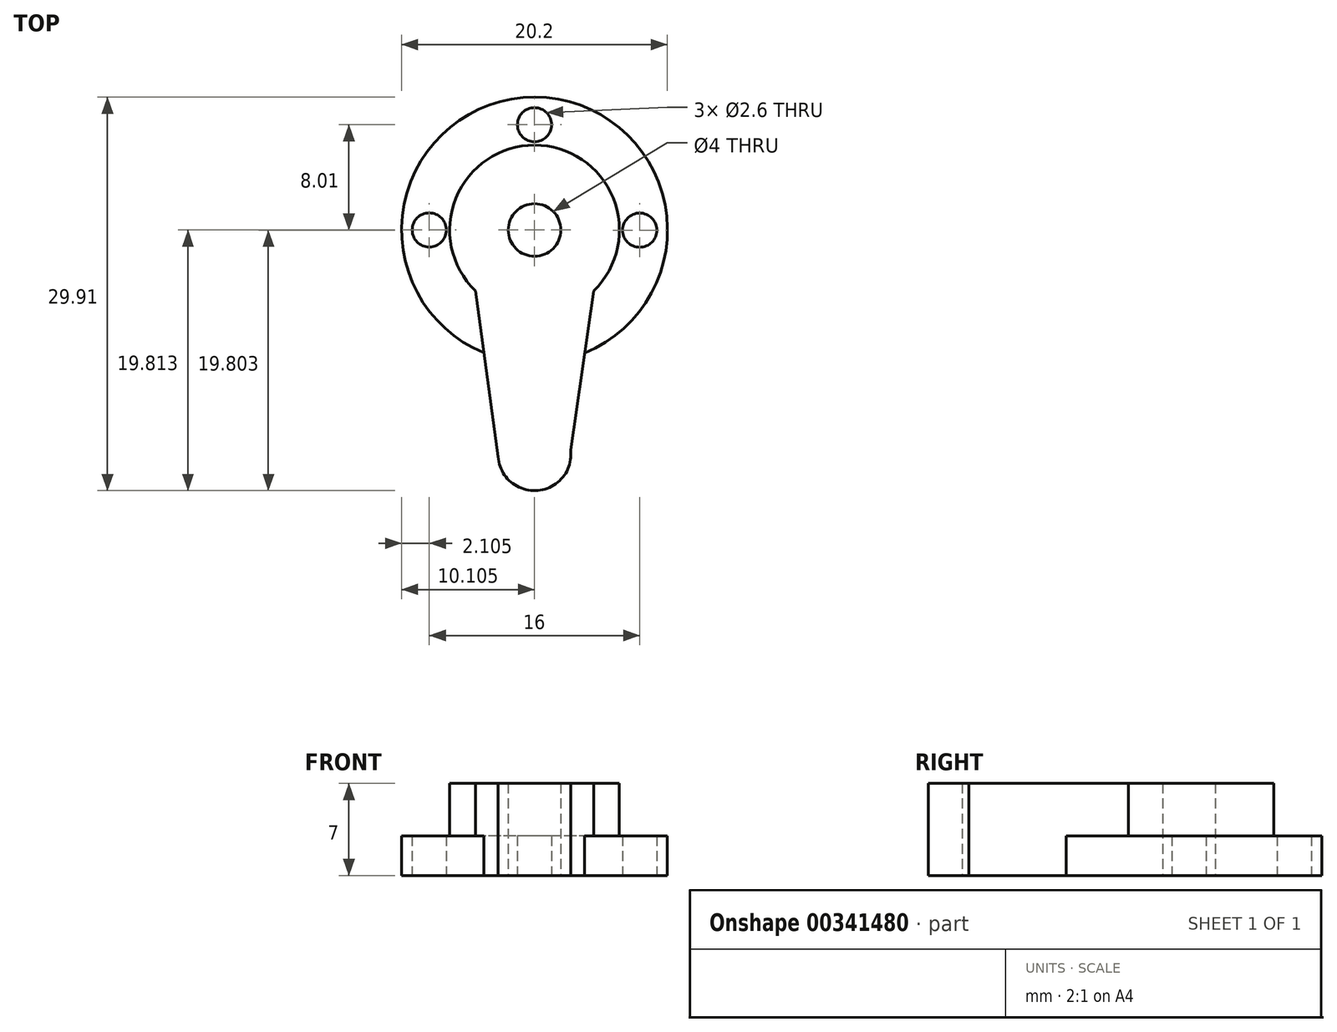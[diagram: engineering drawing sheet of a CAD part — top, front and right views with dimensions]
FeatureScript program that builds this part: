
annotation { "Feature Type Name" : "Feature", "Feature Type Description" : "" }
export const myFeature = defineFeature(function(context is Context, id is Id, definition is map)
    precondition{}
    {
        {
            var Q0;
            Q0=qCreatedBy(makeId("Top.planeOp"),FACE);
            var sketch = newSketch(context, id + "F0", { "sketchPlane" : qUnion([Q0])});
            skCircle(sketch, "E0", {"center": v(-1.19, 10.76) * mm, "radius": 2.77 * mm});
            skPoint(sketch, "E0.first.point", {"position": v(0, 13.26) * mm});
            skPoint(sketch, "E0.second.point", {"position": v(0, 8.26) * mm});
            skPoint(sketch, "E0.third.point", {"position": v(0.69, 8.72) * mm});
            skCircle(sketch, "E1", {"center": v(-1.19, 27.81) * mm, "radius": 6.45 * mm});
            skPoint(sketch, "E1.first.point", {"position": v(-1.19, 34.26) * mm});
            skPoint(sketch, "E1.second.point", {"position": v(-1.19, 21.36) * mm});
            skPoint(sketch, "E1.third.point", {"position": v(4.49, 24.74) * mm});
            skLineSegment(sketch, "E2", {"start": v(-5.69, 23.2) * mm, "end": v(3.31, 23.2) * mm});
            skLineSegment(sketch, "E3", {"start": v(-3.95, 10.57) * mm, "end": v(-5.69, 23.2) * mm});
            skLineSegment(sketch, "E4", {"start": v(1.56, 11.08) * mm, "end": v(3.31, 23.2) * mm});
            skCircle(sketch, "E5", {"center": v(-1.19, 27.81) * mm, "radius": 2 * mm});
            skCircle(sketch, "E6", {"center": v(-1.19, 27.81) * mm, "radius": 10.1 * mm});
            skCircle(sketch, "E7", {"center": v(-1.19, 27.81) * mm, "radius": 8 * mm});
            skCircle(sketch, "E8", {"center": v(-1.19, 35.81) * mm, "radius": 1.3 * mm});
            skLineSegment(sketch, "E9", {"start": v(-1.31, 27.81) * mm, "end": v(5.26, 27.81) * mm});
            skLineSegment(sketch, "E10", {"start": v(5.26, 27.81) * mm, "end": v(6.81, 27.8) * mm});
            skLineSegment(sketch, "E11", {"start": v(-1.19, 27.81) * mm, "end": v(-9.19, 27.81) * mm});
            skCircle(sketch, "E12", {"center": v(6.81, 27.8) * mm, "radius": 1.3 * mm});
            skCircle(sketch, "E13", {"center": v(-9.19, 27.81) * mm, "radius": 1.3 * mm});
            skLineSegment(sketch, "E14", {"start": v(-1.19, 27.81) * mm, "end": v(-1.19, 10.76) * mm});
            skSolve(sketch);
        }
        {
            var Q0;
            {var subQ0=sQuery(id+"F0.wireOp",EDGE,"E2");Q0=makeQuery(id+"F0.imprint","IMPRINT",FACE,{"disambiguationData":[TD([[makeQuery(id+"F0.imprint","IMPRINT",EDGE,{"derivedFrom":subQ0}),-1.0]])]});}
            var Q1;
            {var subQ0=sQuery(id+"F0.wireOp",EDGE,"E2");Q1=makeQuery(id+"F0.imprint","IMPRINT",FACE,{"disambiguationData":[TD([[makeQuery(id+"F0.imprint","IMPRINT",EDGE,{"derivedFrom":subQ0}),1.0]])]});}
            var Q2;
            {var subQ0=sQuery(id+"F0.wireOp",EDGE,"E3");var subQ1=sQuery(id+"F0.wireOp",EDGE,"E0");var subQ2=makeQuery(id+"F0.imprint","INTERSECT",VERTEX,{"derivedFrom":[subQ1,subQ0]});Q2=makeQuery(id+"F0.imprint","IMPRINT",FACE,{"disambiguationData":[TD([[makeQuery(id+"F0.imprint","IMPRINT",EDGE,{"disambiguationData":[TD([[subQ2,1.0]])],"derivedFrom":subQ1}),-1.0]])]});}
            var Q3;
            {var subQ0=sQuery(id+"F0.wireOp",EDGE,"E0");var subQ1=makeQuery(id+"F0.imprint","INTERSECT",VERTEX,{"derivedFrom":[subQ0,sQuery(id+"F0.wireOp",EDGE,"E3")]});Q3=makeQuery(id+"F0.imprint","IMPRINT",FACE,{"disambiguationData":[TD([[makeQuery(id+"F0.imprint","IMPRINT",EDGE,{"disambiguationData":[TD([[subQ1,1.0]])],"derivedFrom":subQ0}),1.0]])]});}
            var Q4;
            {var subQ0=sQuery(id+"F0.wireOp",EDGE,"E6");var subQ1=sQuery(id+"F0.wireOp",EDGE,"E3");var subQ2=makeQuery(id+"F0.imprint","INTERSECT",VERTEX,{"derivedFrom":[subQ1,subQ0]});Q4=makeQuery(id+"F0.imprint","IMPRINT",FACE,{"disambiguationData":[TD([[makeQuery(id+"F0.imprint","IMPRINT",EDGE,{"disambiguationData":[TD([[subQ2,-1.0]])],"derivedFrom":subQ1}),-1.0]])]});}
            var Q5;
            {var subQ0=sQuery(id+"F0.wireOp",EDGE,"E3");var subQ6=sQuery(id+"F0.wireOp",EDGE,"E7");var subQ7=makeQuery(id+"F0.imprint","INTERSECT",VERTEX,{"derivedFrom":[subQ0,subQ6]});Q5=makeQuery(id+"F0.imprint","IMPRINT",FACE,{"disambiguationData":[TD([[makeQuery(id+"F0.imprint","IMPRINT",EDGE,{"disambiguationData":[TD([[subQ7,-1.0]])],"derivedFrom":subQ6}),1.0]])]});}
            var Q6;
            {var subQ5=sQuery(id+"F0.wireOp",EDGE,"E1");var subQ8=sQuery(id+"F0.wireOp",EDGE,"E12");var subQ10=makeQuery(id+"F0.imprint","INTERSECT",VERTEX,{"disambiguationData":[OD(0.0)],"derivedFrom":[subQ5,subQ8]});Q6=makeQuery(id+"F0.imprint","IMPRINT",FACE,{"disambiguationData":[TD([[makeQuery(id+"F0.imprint","IMPRINT",EDGE,{"disambiguationData":[TD([[subQ10,-1.0]])],"derivedFrom":subQ5}),1.0]])]});}
            var Q7;
            {var subQ0=sQuery(id+"F0.wireOp",EDGE,"E9");var subQ1=sQuery(id+"F0.wireOp",EDGE,"E5");var subQ2=makeQuery(id+"F0.imprint","INTERSECT",VERTEX,{"derivedFrom":[subQ1,subQ0]});Q7=makeQuery(id+"F0.imprint","IMPRINT",FACE,{"disambiguationData":[TD([[makeQuery(id+"F0.imprint","IMPRINT",EDGE,{"disambiguationData":[TD([[subQ2,1.0]])],"derivedFrom":subQ1}),-1.0]])]});}
            var Q8;
            {var subQ0=sQuery(id+"F0.wireOp",EDGE,"E4");var subQ1=sQuery(id+"F0.wireOp",EDGE,"E0");var subQ2=makeQuery(id+"F0.imprint","INTERSECT",VERTEX,{"derivedFrom":[subQ1,subQ0]});Q8=makeQuery(id+"F0.imprint","IMPRINT",FACE,{"disambiguationData":[TD([[makeQuery(id+"F0.imprint","IMPRINT",EDGE,{"disambiguationData":[TD([[subQ2,-1.0]])],"derivedFrom":subQ1}),-1.0]])]});}
            var Q9;
            {var subQ0=sQuery(id+"F0.wireOp",EDGE,"E6");var subQ1=sQuery(id+"F0.wireOp",EDGE,"E4");var subQ2=makeQuery(id+"F0.imprint","INTERSECT",VERTEX,{"derivedFrom":[subQ1,subQ0]});Q9=makeQuery(id+"F0.imprint","IMPRINT",FACE,{"disambiguationData":[TD([[makeQuery(id+"F0.imprint","IMPRINT",EDGE,{"disambiguationData":[TD([[subQ2,-1.0]])],"derivedFrom":subQ1}),1.0]])]});}
            var Q10;
            {var subQ0=sQuery(id+"F0.wireOp",EDGE,"E4");var subQ5=sQuery(id+"F0.wireOp",EDGE,"E7");var subQ6=makeQuery(id+"F0.imprint","INTERSECT",VERTEX,{"derivedFrom":[subQ0,subQ5]});Q10=makeQuery(id+"F0.imprint","IMPRINT",FACE,{"disambiguationData":[TD([[makeQuery(id+"F0.imprint","IMPRINT",EDGE,{"disambiguationData":[TD([[subQ6,1.0]])],"derivedFrom":subQ5}),1.0]])]});}
            var Q11;
            {var subQ3=sQuery(id+"F0.wireOp",EDGE,"E11");var subQ5=sQuery(id+"F0.wireOp",EDGE,"E5");var subQ6=makeQuery(id+"F0.imprint","INTERSECT",VERTEX,{"derivedFrom":[subQ5,subQ3]});Q11=makeQuery(id+"F0.imprint","IMPRINT",FACE,{"disambiguationData":[TD([[makeQuery(id+"F0.imprint","IMPRINT",EDGE,{"disambiguationData":[TD([[subQ6,1.0]])],"derivedFrom":subQ5}),-1.0]])]});}
            extrude(context, id + "F1", {"entities" : qUnion([Q0, Q1, Q2, Q3, Q4, Q5, Q6, Q7, Q8, Q9, Q10, Q11]), "depth" : 7 * mm});
        }
        {
            var Q0;
            {var subQ0=sQuery(id+"F0.wireOp",EDGE,"E6");var subQ1=sQuery(id+"F0.wireOp",EDGE,"E3");var subQ2=makeQuery(id+"F0.imprint","INTERSECT",VERTEX,{"derivedFrom":[subQ1,subQ0]});Q0=makeQuery(id+"F0.imprint","IMPRINT",FACE,{"disambiguationData":[TD([[makeQuery(id+"F0.imprint","IMPRINT",EDGE,{"disambiguationData":[TD([[subQ2,-1.0]])],"derivedFrom":subQ1}),1.0]])]});}
            var Q1;
            {var subQ0=sQuery(id+"F0.wireOp",EDGE,"E3");var subQ6=sQuery(id+"F0.wireOp",EDGE,"E7");var subQ7=makeQuery(id+"F0.imprint","INTERSECT",VERTEX,{"derivedFrom":[subQ0,subQ6]});Q1=makeQuery(id+"F0.imprint","IMPRINT",FACE,{"disambiguationData":[TD([[makeQuery(id+"F0.imprint","IMPRINT",EDGE,{"disambiguationData":[TD([[subQ7,1.0]])],"derivedFrom":subQ6}),1.0]])]});}
            extrude(context, id + "F2", {"entities" : qUnion([Q0, Q1]), "operationType" : NewBodyOperationType.ADD, "depth" : 3 * mm});
        }
        {
            var Q0;
            {var subQ0=sQuery(id+"F0.wireOp",EDGE,"E4");var subQ5=sQuery(id+"F0.wireOp",EDGE,"E7");var subQ6=makeQuery(id+"F0.imprint","INTERSECT",VERTEX,{"derivedFrom":[subQ0,subQ5]});Q0=makeQuery(id+"F0.imprint","IMPRINT",FACE,{"disambiguationData":[TD([[makeQuery(id+"F0.imprint","IMPRINT",EDGE,{"disambiguationData":[TD([[subQ6,-1.0]])],"derivedFrom":subQ5}),1.0]])]});}
            var Q1;
            {var subQ0=sQuery(id+"F0.wireOp",EDGE,"E12");var subQ1=sQuery(id+"F0.wireOp",EDGE,"E1");var subQ2=makeQuery(id+"F0.imprint","INTERSECT",VERTEX,{"disambiguationData":[OD(0.0)],"derivedFrom":[subQ1,subQ0]});Q1=makeQuery(id+"F0.imprint","IMPRINT",FACE,{"disambiguationData":[TD([[makeQuery(id+"F0.imprint","IMPRINT",EDGE,{"disambiguationData":[TD([[subQ2,-1.0]])],"derivedFrom":subQ1}),-1.0]])]});}
            var Q2;
            {var subQ0=sQuery(id+"F0.wireOp",EDGE,"E8");var subQ5=sQuery(id+"F0.wireOp",EDGE,"E7");var subQ6=makeQuery(id+"F0.imprint","INTERSECT",VERTEX,{"disambiguationData":[OD(1.0)],"derivedFrom":[subQ5,subQ0]});Q2=makeQuery(id+"F0.imprint","IMPRINT",FACE,{"disambiguationData":[TD([[makeQuery(id+"F0.imprint","IMPRINT",EDGE,{"disambiguationData":[TD([[subQ6,-1.0]])],"derivedFrom":subQ5}),1.0]])]});}
            extrude(context, id + "F3", {"entities" : qUnion([Q0, Q1, Q2]), "operationType" : NewBodyOperationType.ADD, "depth" : 3 * mm});
        }
    });
